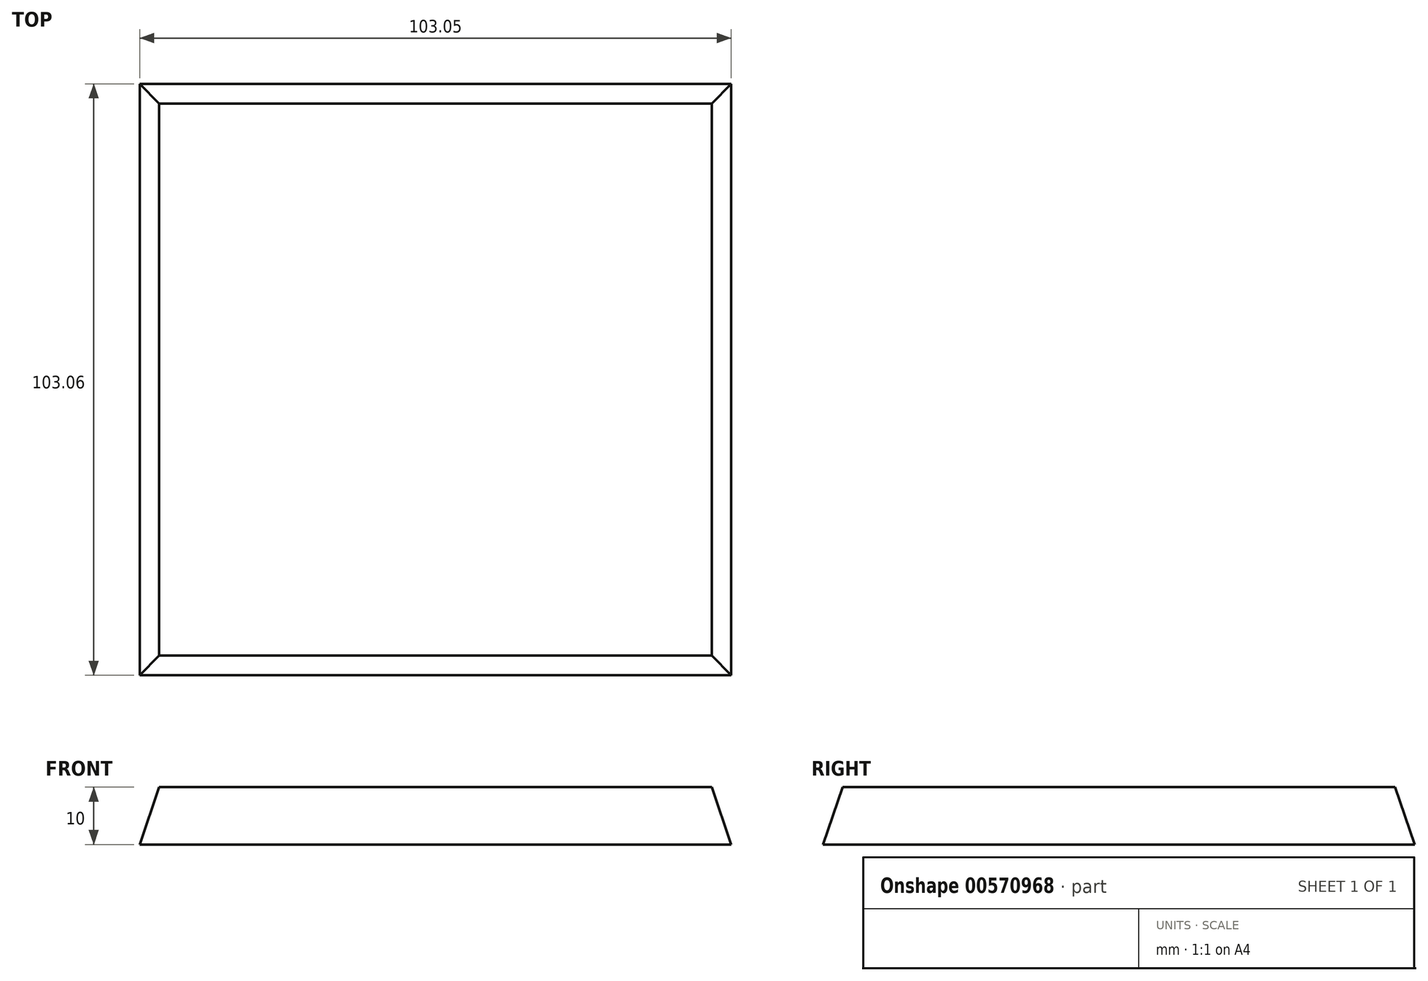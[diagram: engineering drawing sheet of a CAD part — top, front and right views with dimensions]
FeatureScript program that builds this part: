
annotation { "Feature Type Name" : "Feature", "Feature Type Description" : "" }
export const myFeature = defineFeature(function(context is Context, id is Id, definition is map)
    precondition{}
    {
        {
            var Q0;
            Q0=qCreatedBy(makeId("Top.planeOp"),FACE);
            var sketch = newSketch(context, id + "F0", { "sketchPlane" : qUnion([Q0])});
            skLineSegment(sketch, "E0.bottom", {"start": v(-56.44, 55.12) * mm, "end": v(46.61, 55.12) * mm});
            skLineSegment(sketch, "E0.top", {"start": v(-56.44, -47.94) * mm, "end": v(46.61, -47.94) * mm});
            skLineSegment(sketch, "E0.left", {"start": v(-56.44, 55.12) * mm, "end": v(-56.44, -47.94) * mm});
            skLineSegment(sketch, "E0.right", {"start": v(46.61, 55.12) * mm, "end": v(46.61, -47.94) * mm});
            skSolve(sketch);
        }
        {
            var Q0;
            Q0=makeQuery(id+"F0.imprint","IMPRINT",FACE,{"disambiguationData":[TD([[makeQuery(id+"F0.imprint","IMPRINT",EDGE,{"derivedFrom":sQuery(id+"F0.wireOp",EDGE,"E0.bottom")}),-1.0]])]});
            extrude(context, id + "F1", {"entities" : qUnion([Q0]), "depth" : 10 * mm, "offsetDistance" : 25 * mm});
        }
        {
            var Q0;
            Q0=makeQuery(id+"F1.opExtrude","CAP_EDGE",EDGE,{"disambiguationData":[OSD([sQuery(id+"F0.wireOp",EDGE,"E0.right")])],"isStart":false});
            chamfer(context, id + "F2", {"entities" : qUnion([Q0]), "chamferType" : ChamferType.TWO_OFFSETS, "width1" : 10 * mm, "oppositeDirection" : false, "width2" : 3.42 * mm, "tangentPropagation" : true});
        }
        {
            var Q0;
            Q0=makeQuery(id+"F1.opExtrude","CAP_EDGE",EDGE,{"disambiguationData":[OSD([sQuery(id+"F0.wireOp",EDGE,"E0.bottom")])],"isStart":false});
            chamfer(context, id + "F3", {"entities" : qUnion([Q0]), "chamferType" : ChamferType.TWO_OFFSETS, "width1" : 10 * mm, "oppositeDirection" : false, "width2" : 3.42 * mm, "tangentPropagation" : true});
        }
        {
            var Q0;
            Q0=makeQuery(id+"F1.opExtrude","CAP_EDGE",EDGE,{"disambiguationData":[OSD([sQuery(id+"F0.wireOp",EDGE,"E0.top")])],"isStart":false});
            chamfer(context, id + "F4", {"entities" : qUnion([Q0]), "chamferType" : ChamferType.TWO_OFFSETS, "width1" : 10 * mm, "oppositeDirection" : true, "width2" : 3.42 * mm, "tangentPropagation" : true});
        }
        {
            var Q0;
            Q0=makeQuery(id+"F1.opExtrude","CAP_EDGE",EDGE,{"disambiguationData":[OSD([sQuery(id+"F0.wireOp",EDGE,"E0.left")])],"isStart":false});
            chamfer(context, id + "F5", {"entities" : qUnion([Q0]), "chamferType" : ChamferType.TWO_OFFSETS, "width1" : 10 * mm, "oppositeDirection" : true, "width2" : 3.42 * mm, "tangentPropagation" : true});
        }
    });
